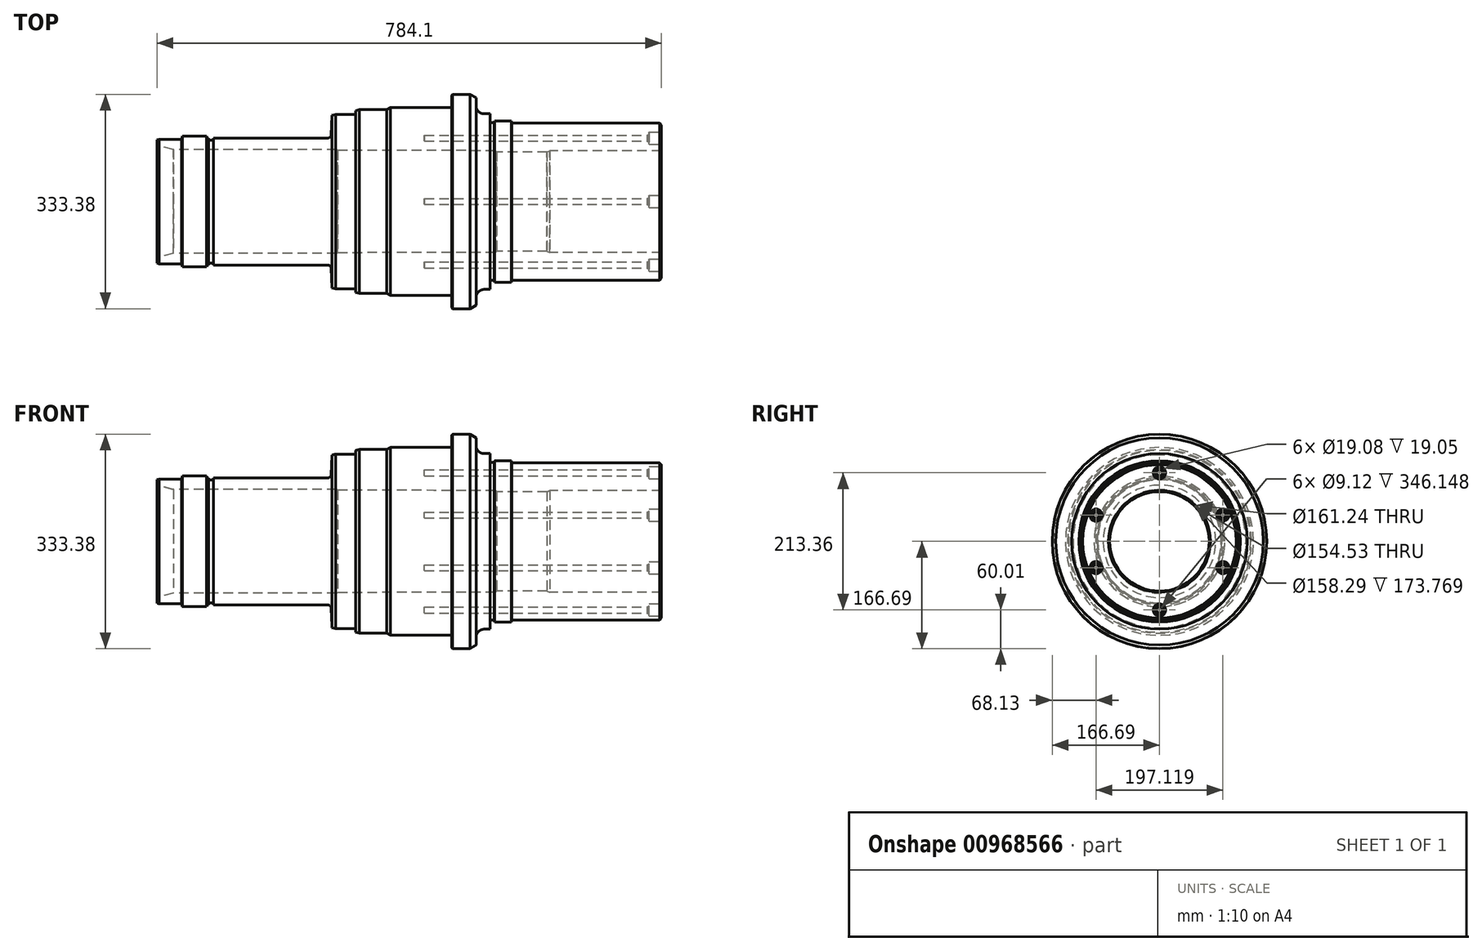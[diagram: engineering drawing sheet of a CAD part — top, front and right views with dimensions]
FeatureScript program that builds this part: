
annotation { "Feature Type Name" : "Feature", "Feature Type Description" : "" }
export const myFeature = defineFeature(function(context is Context, id is Id, definition is map)
    precondition{}
    {
        {
            var Q0;
            Q0=qCreatedBy(makeId("Front.planeOp"),FACE);
            var sketch = newSketch(context, id + "F0", { "sketchPlane" : qUnion([Q0])});
            skLineSegment(sketch, "E0", {"start": v(0, 0) * mm, "end": v(784.1, 0) * mm, "construction": true});
            skLineSegment(sketch, "E1", {"start": v(0, 96.84) * mm, "end": v(38.1, 96.84) * mm});
            skLineSegment(sketch, "E2", {"start": v(25.55, 80.62) * mm, "end": v(279.4, 80.62) * mm});
            skLineSegment(sketch, "E3", {"start": v(39.38, 101.6) * mm, "end": v(77, 101.6) * mm});
            skLineSegment(sketch, "E4", {"start": v(77.72, 98.87) * mm, "end": v(80.16, 98.87) * mm});
            skLineSegment(sketch, "E5", {"start": v(80.16, 98.87) * mm, "end": v(80.16, 95.7) * mm});
            skLineSegment(sketch, "E6", {"start": v(80.16, 95.7) * mm, "end": v(88.09, 95.7) * mm});
            skLineSegment(sketch, "E7", {"start": v(88.09, 95.7) * mm, "end": v(88.09, 98.87) * mm});
            skLineSegment(sketch, "E8", {"start": v(88.09, 98.87) * mm, "end": v(270.59, 98.87) * mm});
            skLineSegment(sketch, "E9", {"start": v(272.2, 135.64) * mm, "end": v(308.69, 135.64) * mm});
            skLineSegment(sketch, "E10", {"start": v(308.69, 135.64) * mm, "end": v(308.69, 142.88) * mm});
            skLineSegment(sketch, "E11", {"start": v(308.69, 142.88) * mm, "end": v(357.2, 142.88) * mm});
            skLineSegment(sketch, "E12", {"start": v(357.2, 142.87) * mm, "end": v(362.7, 146.05) * mm});
            skLineSegment(sketch, "E13", {"start": v(362.7, 146.05) * mm, "end": v(457.99, 146.05) * mm});
            skLineSegment(sketch, "E14", {"start": v(457.99, 146.05) * mm, "end": v(457.99, 166.69) * mm});
            skLineSegment(sketch, "E15", {"start": v(457.99, 166.69) * mm, "end": v(495.94, 166.69) * mm});
            skLineSegment(sketch, "E16", {"start": v(495.94, 166.69) * mm, "end": v(495.94, 136.53) * mm});
            skLineSegment(sketch, "E17", {"start": v(495.94, 136.53) * mm, "end": v(517.52, 136.53) * mm});
            skLineSegment(sketch, "E18", {"start": v(517.52, 136.53) * mm, "end": v(517.52, 122.5) * mm});
            skLineSegment(sketch, "E19", {"start": v(517.52, 122.5) * mm, "end": v(523.88, 122.5) * mm});
            skLineSegment(sketch, "E20", {"start": v(523.88, 122.5) * mm, "end": v(524.65, 125.41) * mm});
            skLineSegment(sketch, "E21", {"start": v(524.65, 125.41) * mm, "end": v(550.85, 125.41) * mm});
            skLineSegment(sketch, "E22", {"start": v(550.85, 125.41) * mm, "end": v(551.7, 122.24) * mm});
            skLineSegment(sketch, "E23", {"start": v(551.7, 122.24) * mm, "end": v(784.1, 122.24) * mm});
            skLineSegment(sketch, "E24", {"start": v(784.1, 79.15) * mm, "end": v(784.1, 122.24) * mm});
            skLineSegment(sketch, "E25", {"start": v(784.1, 79.15) * mm, "end": v(610.33, 79.15) * mm});
            skLineSegment(sketch, "E26", {"start": v(610.33, 79.15) * mm, "end": v(606.3, 77.27) * mm});
            skLineSegment(sketch, "E27", {"start": v(606.3, 77.27) * mm, "end": v(527.92, 77.27) * mm});
            skLineSegment(sketch, "E28", {"start": v(279.4, 80.62) * mm, "end": v(281.23, 79.57) * mm});
            skLineSegment(sketch, "E29", {"start": v(281.23, 79.57) * mm, "end": v(526.04, 79.15) * mm});
            skLineSegment(sketch, "E30", {"start": v(527.92, 77.27) * mm, "end": v(526.04, 79.15) * mm});
            skLineSegment(sketch, "E31", {"start": v(270.59, 98.87) * mm, "end": v(272.2, 135.64) * mm});
            skLineSegment(sketch, "E32", {"start": v(38.1, 96.84) * mm, "end": v(39.38, 101.6) * mm});
            skLineSegment(sketch, "E33", {"start": v(77.72, 98.87) * mm, "end": v(77, 101.6) * mm});
            skPoint(sketch, "E34.end.orphan", {"position": v(38.1, 101.6) * mm});
            skLineSegment(sketch, "E35", {"start": v(0, 87.46) * mm, "end": v(25.55, 80.62) * mm});
            skLineSegment(sketch, "E36", {"start": v(0, 96.84) * mm, "end": v(0, 87.46) * mm});
            skSolve(sketch);
        }
        {
            var Q0;
            Q0=qSketchRegion(id+"F0",true);
            var Q1;
            Q1=sQuery(id+"F0.wireOp",EDGE,"E0");
            revolve(context, id + "F1", {"surfaceOperationType" : NewSurfaceOperationType.NEW, "entities" : qUnion([Q0]), "axis" : qUnion([Q1]), "revolveType" : RevolveType.FULL});
        }
        {
            var Q0;
            Q0=makeQuery(id+"F1.opRevolve","SWEPT_EDGE",EDGE,{"disambiguationData":[OSD([sQuery(id+"F0.wireOp",EDGE,"E15"),sQuery(id+"F0.wireOp",EDGE,"E16")])]});
            chamfer(context, id + "F2", {"entities" : qUnion([Q0]), "chamferType" : ChamferType.OFFSET_ANGLE, "width" : 9.52 * mm, "oppositeDirection" : false, "angle" : 30 * degree, "tangentPropagation" : true});
        }
        {
            var Q0;
            Q0=makeQuery(id+"F1.opRevolve","SWEPT_EDGE",EDGE,{"disambiguationData":[OSD([sQuery(id+"F0.wireOp",EDGE,"E16"),sQuery(id+"F0.wireOp",EDGE,"E17")])]});
            fillet(context, id + "F3", {"entities" : qUnion([Q0]), "radius" : 12.7 * mm, "tangentPropagation" : true, "allowEdgeOverflow" : false});
        }
        {
            var Q0;
            Q0=makeQuery(id+"F1.opRevolve","SWEPT_EDGE",EDGE,{"disambiguationData":[OSD([sQuery(id+"F0.wireOp",EDGE,"E8"),sQuery(id+"F0.wireOp",EDGE,"E31")])]});
            fillet(context, id + "F4", {"entities" : qUnion([Q0]), "radius" : 5.08 * mm, "tangentPropagation" : true, "allowEdgeOverflow" : false});
        }
        {
            var Q0;
            Q0=makeQuery(id+"F1.opRevolve","SWEPT_EDGE",EDGE,{"disambiguationData":[OSD([sQuery(id+"F0.wireOp",EDGE,"E9"),sQuery(id+"F0.wireOp",EDGE,"E31")])]});
            var Q1;
            Q1=makeQuery(id+"F1.opRevolve","SWEPT_EDGE",EDGE,{"disambiguationData":[OSD([sQuery(id+"F0.wireOp",EDGE,"E10"),sQuery(id+"F0.wireOp",EDGE,"E11")])]});
            chamfer(context, id + "F5", {"entities" : qUnion([Q0, Q1]), "chamferType" : ChamferType.OFFSET_ANGLE, "width" : 1.27 * mm, "oppositeDirection" : false, "angle" : 75 * degree, "tangentPropagation" : true});
        }
        {
            var Q0;
            Q0=makeQuery(id+"F1.opRevolve","SWEPT_EDGE",EDGE,{"disambiguationData":[OSD([sQuery(id+"F0.wireOp",EDGE,"E1"),sQuery(id+"F0.wireOp",EDGE,"SCYpA8kQ-7sTV-xUNJ-m1pp-K6qHX3d4gstn")])]});
            chamfer(context, id + "F6", {"entities" : qUnion([Q0]), "chamferType" : ChamferType.OFFSET_ANGLE, "width" : 0.86 * mm, "oppositeDirection" : false, "angle" : 75 * degree, "tangentPropagation" : true});
        }
        {
            var Q0;
            Q0=makeQuery(id+"F1.opRevolve","SWEPT_EDGE",EDGE,{"disambiguationData":[OSD([sQuery(id+"F0.wireOp",EDGE,"E23"),sQuery(id+"F0.wireOp",EDGE,"E24")])]});
            chamfer(context, id + "F7", {"entities" : qUnion([Q0]), "width" : 3.05 * mm, "tangentPropagation" : true});
        }
        {
            var Q0;
            Q0=makeQuery(id+"F1.opRevolve","SWEPT_EDGE",EDGE,{"disambiguationData":[OSD([sQuery(id+"F0.wireOp",EDGE,"E14"),sQuery(id+"F0.wireOp",EDGE,"E15")])]});
            chamfer(context, id + "F8", {"entities" : qUnion([Q0]), "width" : 1.52 * mm, "tangentPropagation" : true});
        }
        {
            var Q0;
            Q0=makeQuery(id+"F1.opRevolve","SWEPT_FACE",FACE,{"disambiguationData":[OSD([sQuery(id+"F0.wireOp",EDGE,"E24")])]});
            var sketch = newSketch(context, id + "F9", { "sketchPlane" : qUnion([Q0])});
            skCircle(sketch, "E37", {"center": v(0, 106.68) * mm, "radius": 4.56 * mm});
            skCircle(sketch, "E38", {"center": v(0, -106.68) * mm, "radius": 4.56 * mm});
            skCircle(sketch, "E39", {"center": v(98.52, 40.92) * mm, "radius": 4.56 * mm});
            skCircle(sketch, "E40", {"center": v(98.56, -40.82) * mm, "radius": 4.56 * mm});
            skCircle(sketch, "E41", {"center": v(-98.56, -40.82) * mm, "radius": 4.56 * mm});
            skCircle(sketch, "E42", {"center": v(-98.56, 40.83) * mm, "radius": 4.56 * mm});
            skLineSegment(sketch, "E43", {"start": v(-107.72, 0) * mm, "end": v(113.39, 0) * mm, "construction": true});
            skLineSegment(sketch, "E44", {"start": v(0, 0) * mm, "end": v(98.52, 40.92) * mm, "construction": true});
            skLineSegment(sketch, "E45", {"start": v(0, 0) * mm, "end": v(-98.56, 40.83) * mm, "construction": true});
            skLineSegment(sketch, "E46", {"start": v(0, 0) * mm, "end": v(-98.56, -40.82) * mm, "construction": true});
            skLineSegment(sketch, "E47", {"start": v(0, 0) * mm, "end": v(98.56, -40.82) * mm, "construction": true});
            skSolve(sketch);
        }
        {
            var Q0;
            Q0=qSketchRegion(id+"F9",true);
            extrude(context, id + "F10", {"entities" : qUnion([Q0]), "operationType" : NewBodyOperationType.REMOVE, "oppositeDirection" : true, "depth" : 368.3 * mm, "offsetDistance" : 25.4 * mm});
        }
        {
            var Q0;
            Q0=makeQuery(id+"F1.opRevolve","SWEPT_FACE",FACE,{"disambiguationData":[OSD([sQuery(id+"F0.wireOp",EDGE,"E24")])]});
            var sketch = newSketch(context, id + "F11", { "sketchPlane" : qUnion([Q0])});
            skCircle(sketch, "E48", {"center": v(98.52, 40.92) * mm, "radius": 9.54 * mm});
            skCircle(sketch, "E49", {"center": v(0, 106.68) * mm, "radius": 9.54 * mm});
            skCircle(sketch, "E50", {"center": v(-98.56, 40.83) * mm, "radius": 9.54 * mm});
            skCircle(sketch, "E51", {"center": v(-98.56, -40.82) * mm, "radius": 9.54 * mm});
            skCircle(sketch, "E52", {"center": v(98.56, -40.82) * mm, "radius": 9.54 * mm});
            skCircle(sketch, "E53", {"center": v(0, -106.68) * mm, "radius": 9.54 * mm});
            skSolve(sketch);
        }
        {
            var Q0;
            Q0=qSketchRegion(id+"F11",true);
            extrude(context, id + "F12", {"entities" : qUnion([Q0]), "operationType" : NewBodyOperationType.REMOVE, "oppositeDirection" : true, "depth" : 19.05 * mm, "offsetDistance" : 25.4 * mm});
        }
        {
            var Q0;
            Q0=makeQuery(id+"F12.boolean.opBoolean","INTERSECT",EDGE,{"derivedFrom":[makeQuery(id+"F10.boolean.opBoolean","COPY",FACE,{"derivedFrom":makeQuery(id+"F10.opExtrude","SWEPT_FACE",FACE,{"disambiguationData":[OSD([sQuery(id+"F9.wireOp",EDGE,"E37")])]})}),makeQuery(id+"F12.opExtrude","CAP_FACE",FACE,{"disambiguationData":[OSD([sQuery(id+"F11.wireOp",EDGE,"E49")])],"isStart":false})]});
            var Q1;
            Q1=makeQuery(id+"F12.boolean.opBoolean","INTERSECT",EDGE,{"derivedFrom":[makeQuery(id+"F10.boolean.opBoolean","COPY",FACE,{"derivedFrom":makeQuery(id+"F10.opExtrude","SWEPT_FACE",FACE,{"disambiguationData":[OSD([sQuery(id+"F9.wireOp",EDGE,"E42")])]})}),makeQuery(id+"F12.opExtrude","CAP_FACE",FACE,{"disambiguationData":[OSD([sQuery(id+"F11.wireOp",EDGE,"E50")])],"isStart":false})]});
            var Q2;
            Q2=makeQuery(id+"F12.boolean.opBoolean","INTERSECT",EDGE,{"derivedFrom":[makeQuery(id+"F10.boolean.opBoolean","COPY",FACE,{"derivedFrom":makeQuery(id+"F10.opExtrude","SWEPT_FACE",FACE,{"disambiguationData":[OSD([sQuery(id+"F9.wireOp",EDGE,"E38")])]})}),makeQuery(id+"F12.opExtrude","CAP_FACE",FACE,{"disambiguationData":[OSD([sQuery(id+"F11.wireOp",EDGE,"E53")])],"isStart":false})]});
            var Q3;
            Q3=makeQuery(id+"F12.boolean.opBoolean","INTERSECT",EDGE,{"derivedFrom":[makeQuery(id+"F10.boolean.opBoolean","COPY",FACE,{"derivedFrom":makeQuery(id+"F10.opExtrude","SWEPT_FACE",FACE,{"disambiguationData":[OSD([sQuery(id+"F9.wireOp",EDGE,"E41")])]})}),makeQuery(id+"F12.opExtrude","CAP_FACE",FACE,{"disambiguationData":[OSD([sQuery(id+"F11.wireOp",EDGE,"E51")])],"isStart":false})]});
            var Q4;
            Q4=makeQuery(id+"F12.boolean.opBoolean","INTERSECT",EDGE,{"derivedFrom":[makeQuery(id+"F10.boolean.opBoolean","COPY",FACE,{"derivedFrom":makeQuery(id+"F10.opExtrude","SWEPT_FACE",FACE,{"disambiguationData":[OSD([sQuery(id+"F9.wireOp",EDGE,"E40")])]})}),makeQuery(id+"F12.opExtrude","CAP_FACE",FACE,{"disambiguationData":[OSD([sQuery(id+"F11.wireOp",EDGE,"E52")])],"isStart":false})]});
            var Q5;
            Q5=makeQuery(id+"F12.boolean.opBoolean","INTERSECT",EDGE,{"derivedFrom":[makeQuery(id+"F10.boolean.opBoolean","COPY",FACE,{"derivedFrom":makeQuery(id+"F10.opExtrude","SWEPT_FACE",FACE,{"disambiguationData":[OSD([sQuery(id+"F9.wireOp",EDGE,"E39")])]})}),makeQuery(id+"F12.opExtrude","CAP_FACE",FACE,{"disambiguationData":[OSD([sQuery(id+"F11.wireOp",EDGE,"E48")])],"isStart":false})]});
            chamfer(context, id + "F13", {"entities" : qUnion([Q0, Q1, Q2, Q3, Q4, Q5]), "chamferType" : ChamferType.OFFSET_ANGLE, "width" : 1.8 * mm, "oppositeDirection" : false, "angle" : 60 * degree, "tangentPropagation" : true});
        }
    });
